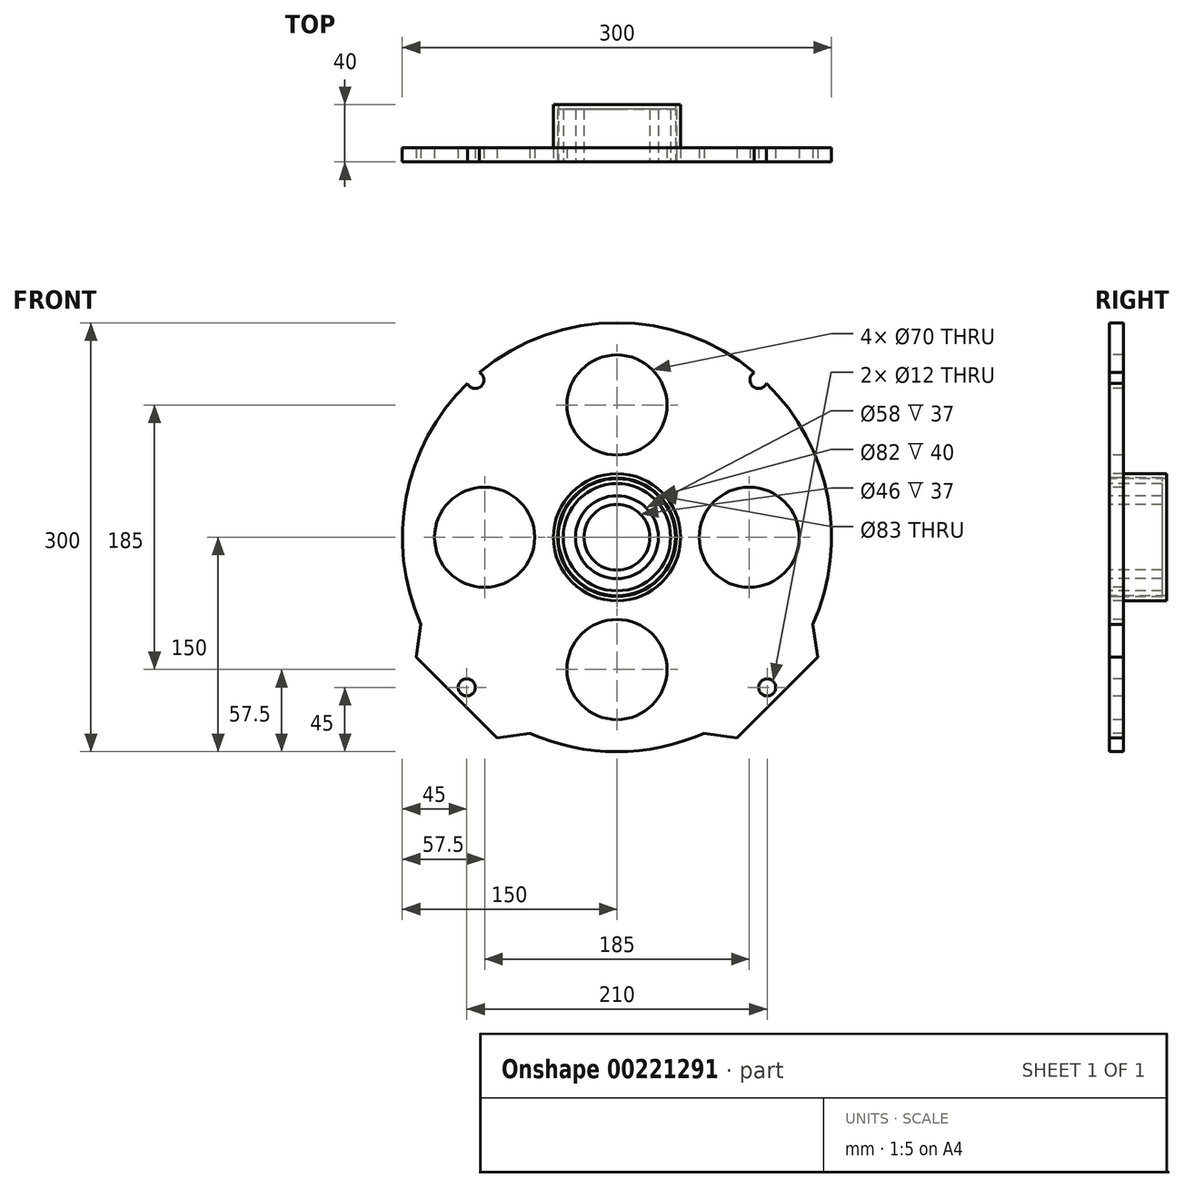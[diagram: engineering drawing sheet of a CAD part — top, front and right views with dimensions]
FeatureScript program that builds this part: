
annotation { "Feature Type Name" : "Feature", "Feature Type Description" : "" }
export const myFeature = defineFeature(function(context is Context, id is Id, definition is map)
    precondition{}
    {
        {
            var Q0;
            Q0=qCreatedBy(makeId("Front.planeOp"),FACE);
            var sketch = newSketch(context, id + "F0", { "sketchPlane" : qUnion([Q0])});
            skCircle(sketch, "E0", {"center": v(0, 0) * mm, "radius": 150 * mm});
            skCircle(sketch, "E1", {"center": v(0, 0) * mm, "radius": 140 * mm});
            skCircle(sketch, "E2", {"center": v(-99, 110) * mm, "radius": 6 * mm});
            skCircle(sketch, "E3.MirrorC", {"center": v(99, 110) * mm, "radius": 6 * mm});
            skCircle(sketch, "E4", {"center": v(105, -105) * mm, "radius": 6 * mm});
            skCircle(sketch, "E5.MirrorC", {"center": v(-105, -105) * mm, "radius": 6 * mm});
            skArc(sketch, "E6", {"start": v(-108.87, 103.18) * mm, "mid": v(-107.03, 118.92) * mm, "end": v(-91.18, 119.1) * mm});
            skArc(sketch, "E7", {"start": v(91.18, 119.1) * mm, "mid": v(107.03, 118.92) * mm, "end": v(108.87, 103.18) * mm});
            skLineSegment(sketch, "E8", {"start": v(-105, -105) * mm, "end": v(-112.07, -112.07) * mm});
            skLineSegment(sketch, "E9", {"start": v(-112.07, -112.07) * mm, "end": v(-83.79, -140.36) * mm});
            skLineSegment(sketch, "E10.MirrorCS", {"start": v(-112.07, -112.07) * mm, "end": v(-140.36, -83.79) * mm});
            skLineSegment(sketch, "E11", {"start": v(-140.36, -83.79) * mm, "end": v(-137.02, -61.03) * mm});
            skLineSegment(sketch, "E12.MirrorCS", {"start": v(-83.79, -140.36) * mm, "end": v(-61.03, -137.02) * mm});
            skLineSegment(sketch, "E13.MirrorCS", {"start": v(140.36, -83.79) * mm, "end": v(137.02, -61.03) * mm});
            skLineSegment(sketch, "E14.MirrorCS", {"start": v(112.07, -112.07) * mm, "end": v(140.36, -83.79) * mm});
            skLineSegment(sketch, "E15.MirrorCS", {"start": v(112.07, -112.07) * mm, "end": v(83.79, -140.36) * mm});
            skLineSegment(sketch, "E16.MirrorCS", {"start": v(83.79, -140.36) * mm, "end": v(61.03, -137.02) * mm});
            skCircle(sketch, "E17", {"center": v(0, 0) * mm, "radius": 41.5 * mm});
            skCircle(sketch, "E18", {"center": v(0, 92.5) * mm, "radius": 35 * mm});
            skCircle(sketch, "E19.MirrorC", {"center": v(0, -92.5) * mm, "radius": 35 * mm});
            skCircle(sketch, "E20", {"center": v(0, 0) * mm, "radius": 92.5 * mm});
            skCircle(sketch, "E21", {"center": v(92.5, 0) * mm, "radius": 35 * mm});
            skCircle(sketch, "E22", {"center": v(-92.5, 0) * mm, "radius": 35 * mm});
            skSolve(sketch);
        }
        {
            var Q0;
            Q0=makeQuery(id+"F0.imprint","IMPRINT",FACE,{"disambiguationData":[TD([[makeQuery(id+"F0.imprint","IMPRINT",EDGE,{"derivedFrom":sQuery(id+"F0.wireOp",EDGE,"E1")}),1.0]])]});
            var sketch = newSketch(context, id + "F1", { "sketchPlane" : qUnion([Q0])});
            skCircle(sketch, "E23", {"center": v(0, 0) * mm, "radius": 44.45 * mm});
            skCircle(sketch, "E24", {"center": v(0, 0) * mm, "radius": 41 * mm});
            skSolve(sketch);
        }
        {
            var Q0;
            Q0=makeQuery(id+"F0.imprint","IMPRINT",FACE,{"disambiguationData":[TD([[makeQuery(id+"F0.imprint","IMPRINT",EDGE,{"derivedFrom":sQuery(id+"F0.wireOp",EDGE,"E1")}),1.0]])]});
            var sketch = newSketch(context, id + "F2", { "sketchPlane" : qUnion([Q0])});
            skCircle(sketch, "E25", {"center": v(0, 0) * mm, "radius": 41 * mm});
            skCircle(sketch, "E26", {"center": v(0, 0) * mm, "radius": 37.5 * mm});
            skCircle(sketch, "E27", {"center": v(0, 0) * mm, "radius": 29 * mm});
            skCircle(sketch, "E28", {"center": v(0, 0) * mm, "radius": 23 * mm});
            skSolve(sketch);
        }
        {
            var Q0;
            Q0=makeQuery(id+"F2.imprint","IMPRINT",FACE,{"disambiguationData":[TD([[makeQuery(id+"F2.imprint","IMPRINT",EDGE,{"derivedFrom":sQuery(id+"F2.wireOp",EDGE,"E27")}),1.0]])]});
            extrude(context, id + "F3", {"entities" : qUnion([Q0]), "oppositeDirection" : true, "depth" : 37 * mm});
        }
        {
            var Q0;
            Q0=makeQuery(id+"F2.imprint","IMPRINT",FACE,{"disambiguationData":[TD([[makeQuery(id+"F2.imprint","IMPRINT",EDGE,{"derivedFrom":sQuery(id+"F2.wireOp",EDGE,"E26")}),1.0]])]});
            extrude(context, id + "F4", {"entities" : qUnion([Q0]), "oppositeDirection" : true, "depth" : 37 * mm});
        }
        {
            var Q0;
            Q0=makeQuery(id+"F1.imprint","IMPRINT",FACE,{"disambiguationData":[TD([[makeQuery(id+"F1.imprint","IMPRINT",EDGE,{"derivedFrom":sQuery(id+"F1.wireOp",EDGE,"E23")}),1.0]])]});
            extrude(context, id + "F5", {"entities" : qUnion([Q0]), "oppositeDirection" : true, "depth" : 40 * mm});
        }
        {
            var Q0;
            Q0=makeQuery(id+"F0.imprint","IMPRINT",FACE,{"disambiguationData":[TD([[makeQuery(id+"F0.imprint","IMPRINT",EDGE,{"derivedFrom":sQuery(id+"F0.wireOp",EDGE,"E1")}),1.0]])]});
            var Q1;
            Q1=makeQuery(id+"F0.imprint","IMPRINT",FACE,{"disambiguationData":[TD([[makeQuery(id+"F0.imprint","IMPRINT",EDGE,{"derivedFrom":sQuery(id+"F0.wireOp",EDGE,"E17")}),-1.0]])]});
            var Q2;
            {var subQ0=sQuery(id+"F0.wireOp",EDGE,"E9");Q2=makeQuery(id+"F0.imprint","IMPRINT",FACE,{"disambiguationData":[TD([[makeQuery(id+"F0.imprint","IMPRINT",EDGE,{"derivedFrom":subQ0}),1.0]])]});}
            var Q3;
            Q3=makeQuery(id+"F0.imprint","IMPRINT",FACE,{"disambiguationData":[TD([[makeQuery(id+"F0.imprint","IMPRINT",EDGE,{"derivedFrom":sQuery(id+"F0.wireOp",EDGE,"E1")}),-1.0]])]});
            var Q4;
            {var subQ0=sQuery(id+"F0.wireOp",EDGE,"E10.MirrorCS");Q4=makeQuery(id+"F0.imprint","IMPRINT",FACE,{"disambiguationData":[TD([[makeQuery(id+"F0.imprint","IMPRINT",EDGE,{"derivedFrom":subQ0}),-1.0]])]});}
            var Q5;
            {var subQ0=sQuery(id+"F0.wireOp",EDGE,"E13.MirrorCS");Q5=makeQuery(id+"F0.imprint","IMPRINT",FACE,{"disambiguationData":[TD([[makeQuery(id+"F0.imprint","IMPRINT",EDGE,{"derivedFrom":subQ0}),1.0]])]});}
            var Q6;
            {var subQ0=sQuery(id+"F0.wireOp",EDGE,"E7");Q6=makeQuery(id+"F0.imprint","IMPRINT",FACE,{"disambiguationData":[TD([[makeQuery(id+"F0.imprint","IMPRINT",EDGE,{"derivedFrom":subQ0}),-1.0]])]});}
            var Q7;
            {var subQ0=sQuery(id+"F0.wireOp",EDGE,"E6");Q7=makeQuery(id+"F0.imprint","IMPRINT",FACE,{"disambiguationData":[TD([[makeQuery(id+"F0.imprint","IMPRINT",EDGE,{"derivedFrom":subQ0}),-1.0]])]});}
            extrude(context, id + "F6", {"entities" : qUnion([Q0, Q1, Q2, Q3, Q4, Q5, Q6, Q7]), "oppositeDirection" : true, "depth" : 10 * mm});
        }
        {
            var Q0;
            Q0=makeQuery(id+"F0.imprint","IMPRINT",FACE,{"disambiguationData":[TD([[makeQuery(id+"F0.imprint","IMPRINT",EDGE,{"derivedFrom":sQuery(id+"F0.wireOp",EDGE,"E17")}),1.0]])]});
            extrude(context, id + "F7", {"entities" : qUnion([Q0]), "oppositeDirection" : true, "depth" : 37 * mm});
        }
    });
